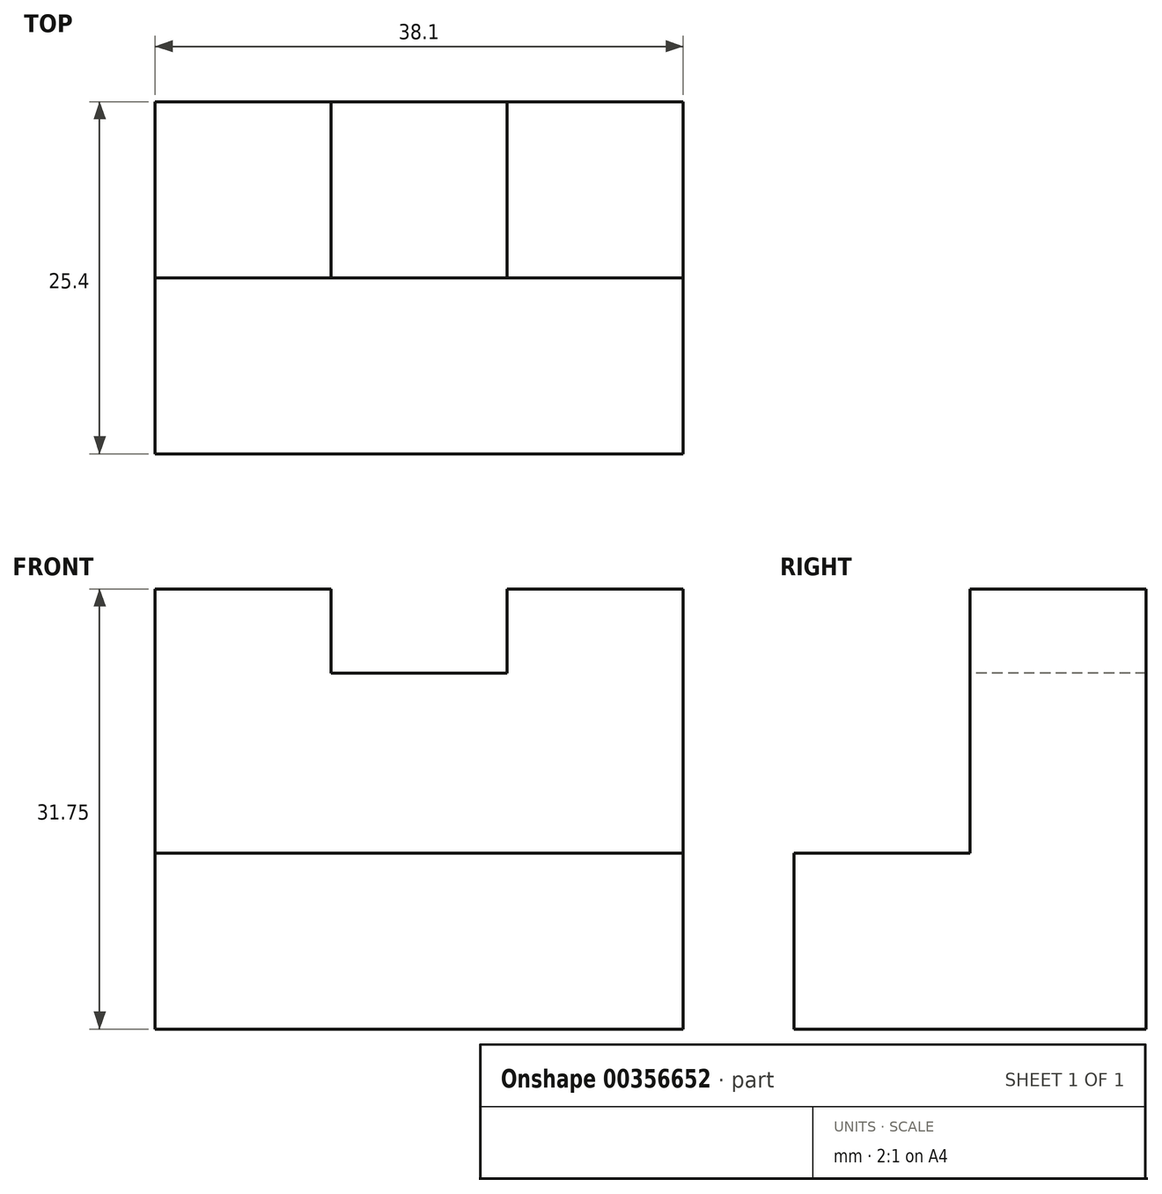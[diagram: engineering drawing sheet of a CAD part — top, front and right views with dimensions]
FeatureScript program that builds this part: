
annotation { "Feature Type Name" : "Feature", "Feature Type Description" : "" }
export const myFeature = defineFeature(function(context is Context, id is Id, definition is map)
    precondition{}
    {
        {
            var Q0;
            Q0=qCreatedBy(makeId("Right.planeOp"),FACE);
            var sketch = newSketch(context, id + "F0", { "sketchPlane" : qUnion([Q0])});
            skLineSegment(sketch, "E0", {"start": v(15.49, -15.6) * mm, "end": v(15.49, -47.35) * mm});
            skLineSegment(sketch, "E1", {"start": v(15.49, -47.35) * mm, "end": v(-9.91, -47.35) * mm});
            skLineSegment(sketch, "E2", {"start": v(-9.91, -47.35) * mm, "end": v(-9.91, -34.65) * mm});
            skLineSegment(sketch, "E3", {"start": v(-9.91, -34.65) * mm, "end": v(2.79, -34.65) * mm});
            skLineSegment(sketch, "E4", {"start": v(2.79, -34.65) * mm, "end": v(2.79, -15.6) * mm});
            skLineSegment(sketch, "E5", {"start": v(2.79, -15.6) * mm, "end": v(15.49, -15.6) * mm});
            skSolve(sketch);
        }
        {
            var Q0;
            Q0 = qSketchRegion(id + "F0", true);
            extrude(context, id + "F1", {"entities" : qUnion([Q0]), "depth" : 38.1 * mm});
        }
        {
            var Q0;
            Q0=qCreatedBy(makeId("Front.planeOp"),FACE);
            var sketch = newSketch(context, id + "F2", { "sketchPlane" : qUnion([Q0])});
            skLineSegment(sketch, "E6", {"start": v(12.7, -15.32) * mm, "end": v(12.7, -21.67) * mm});
            skLineSegment(sketch, "E7", {"start": v(12.7, -21.67) * mm, "end": v(25.4, -21.67) * mm});
            skLineSegment(sketch, "E8", {"start": v(25.4, -21.67) * mm, "end": v(25.4, -15.32) * mm});
            skLineSegment(sketch, "E9", {"start": v(12.7, -15.32) * mm, "end": v(25.4, -15.32) * mm});
            skSolve(sketch);
        }
        {
            var Q0;
            Q0 = qSketchRegion(id + "F2", true);
            extrude(context, id + "F3", {"entities" : qUnion([Q0]), "operationType" : NewBodyOperationType.REMOVE, "endBound" : BoundingType.THROUGH_ALL, "oppositeDirection" : true, "depth" : 12.7 * mm});
        }
    });
